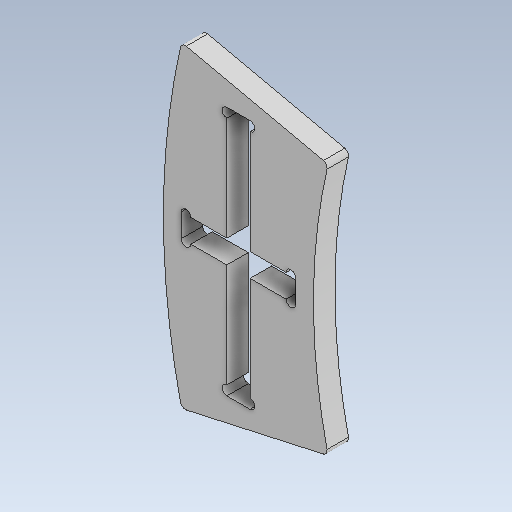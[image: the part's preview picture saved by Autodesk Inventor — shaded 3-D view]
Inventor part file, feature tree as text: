
AUTODESK INVENTOR PART (.ipt)
format: ipt  version: 2020 (Build 240168000, 168)  size: 153,088 bytes
history: native  units: mm
features: extrude x1, fillet x1, sketch x1
ambient origin geometry x8: Origin, YZ Plane, XZ Plane, XY Plane, X Axis, Y Axis, Z Axis, Center Point
bodies: Solid1 (feature_tree)
feature tree (3):
  extrude  "Extrusion1"  Depth=1.333333mm
  fillet  "Fillet1"  Radius=2.666667mm
  sketch  "Sketch1"  dims[d1=6.5mm d3=1.333333mm d4=2.666667mm d10=0.0mm d11=0.0mm d14=2.666667mm d15=1.333333mm d26=392.0mm d30=5.0mm d31=6.0mm d32=0.0mm d33=1.333333mm d38=0.0mm d40=10.096987mm d41=0.0mm d42=3.25mm d43=0.0mm]
